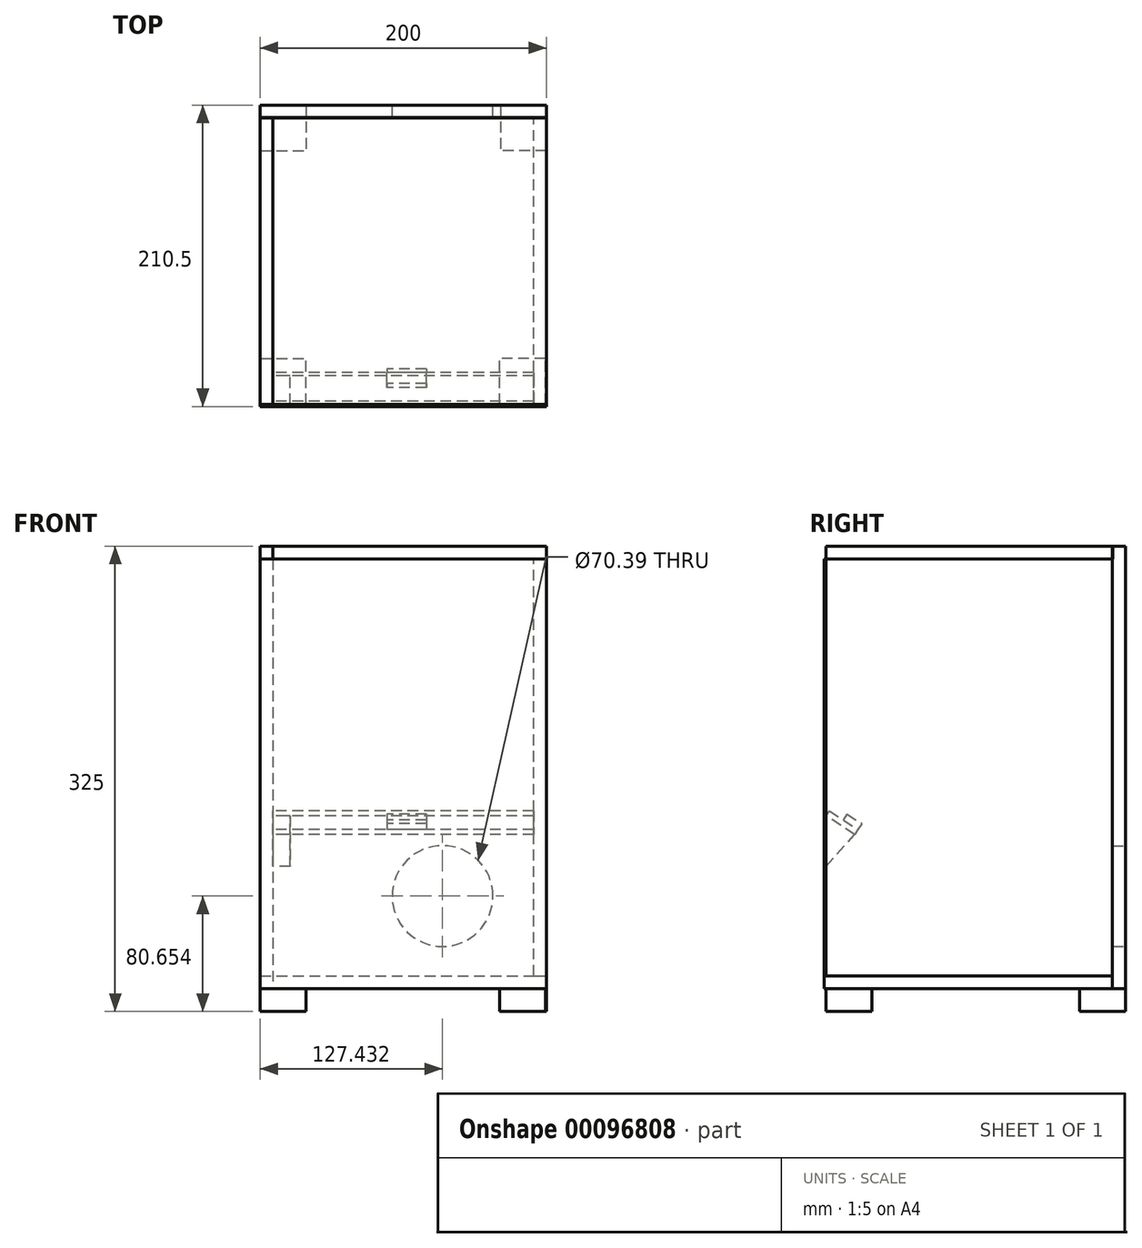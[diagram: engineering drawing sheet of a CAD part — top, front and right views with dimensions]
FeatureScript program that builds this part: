
annotation { "Feature Type Name" : "Feature", "Feature Type Description" : "" }
export const myFeature = defineFeature(function(context is Context, id is Id, definition is map)
    precondition{}
    {
        {
            var Q0;
            Q0=qCreatedBy(makeId("Front.planeOp"),FACE);
            var sketch = newSketch(context, id + "F0", { "sketchPlane" : qUnion([Q0])});
            skLineSegment(sketch, "E0.bottom", {"start": v(0, 0) * mm, "end": v(200, 0) * mm});
            skLineSegment(sketch, "E0.top", {"start": v(0, 300) * mm, "end": v(200, 300) * mm});
            skLineSegment(sketch, "E0.left", {"start": v(0, 0) * mm, "end": v(0, 300) * mm});
            skLineSegment(sketch, "E0.right", {"start": v(200, 0) * mm, "end": v(200, 300) * mm});
            skSolve(sketch);
        }
        {
            var Q0;
            Q0=makeQuery(id+"F0.imprint","IMPRINT",FACE,{"disambiguationData":[TD([[makeQuery(id+"F0.imprint","IMPRINT",EDGE,{"derivedFrom":sQuery(id+"F0.wireOp",EDGE,"E0.bottom")}),1.0]])]});
            var Q1;
            Q1=makeQuery(id+"F0.imprint","IMPRINT",FACE,{"disambiguationData":[TD([[makeQuery(id+"F0.imprint","IMPRINT",EDGE,{"derivedFrom":sQuery(id+"F0.wireOp",EDGE,"E0.bottom")}),1.0]])]});
            extrude(context, id + "F1", {"entities" : qUnion([Q0, Q1]), "depth" : 1.5 * mm});
        }
        {
            var Q0;
            Q0=makeQuery(id+"F1.opExtrude","CAP_FACE",FACE,{"disambiguationData":[OSD([sQuery(id+"F0.wireOp",EDGE,"E0.bottom"),sQuery(id+"F0.wireOp",EDGE,"E0.top"),sQuery(id+"F0.wireOp",EDGE,"E0.left"),sQuery(id+"F0.wireOp",EDGE,"E0.right")])],"isStart":true});
            var sketch = newSketch(context, id + "F2", { "sketchPlane" : qUnion([Q0])});
            skLineSegment(sketch, "E1.bottom", {"start": v(0, 300) * mm, "end": v(-9, 300) * mm});
            skLineSegment(sketch, "E1.top", {"start": v(0, 0) * mm, "end": v(-9, 0) * mm});
            skLineSegment(sketch, "E1.left", {"start": v(0, 300) * mm, "end": v(0, 0) * mm});
            skLineSegment(sketch, "E1.right", {"start": v(-9, 300) * mm, "end": v(-9, 0) * mm});
            skSolve(sketch);
        }
        {
            var Q0;
            Q0 = qSketchRegion(id + "F2", true);
            extrude(context, id + "F3", {"entities" : qUnion([Q0]), "depth" : 200 * mm});
        }
        {
            var Q0;
            Q0=makeQuery(id+"F3.opExtrude","SWEPT_FACE",FACE,{"disambiguationData":[OSD([sQuery(id+"F2.wireOp",EDGE,"E1.right")])]});
            var sketch = newSketch(context, id + "F4", { "sketchPlane" : qUnion([Q0])});
            skLineSegment(sketch, "E2", {"start": v(0, 120.62) * mm, "end": v(0, 85.37) * mm});
            skLineSegment(sketch, "E3", {"start": v(0, 85.37) * mm, "end": v(19.83, 107.63) * mm});
            skLineSegment(sketch, "E4", {"start": v(19.83, 107.63) * mm, "end": v(0, 120.62) * mm});
            skSolve(sketch);
        }
        {
            var Q0;
            Q0 = qSketchRegion(id + "F4", true);
            extrude(context, id + "F5", {"entities" : qUnion([Q0]), "depth" : 12 * mm});
        }
        {
            var Q0;
            Q0=makeQuery(id+"F3.opExtrude","SWEPT_FACE",FACE,{"disambiguationData":[OSD([sQuery(id+"F2.wireOp",EDGE,"E1.right")])]});
            var sketch = newSketch(context, id + "F6", { "sketchPlane" : qUnion([Q0])});
            skLineSegment(sketch, "E5", {"start": v(19.83, 107.63) * mm, "end": v(0, 120.62) * mm});
            skLineSegment(sketch, "E6", {"start": v(0, 120.62) * mm, "end": v(2.3, 124.14) * mm});
            skLineSegment(sketch, "E7", {"start": v(2.3, 124.14) * mm, "end": v(22.14, 111.15) * mm});
            skLineSegment(sketch, "E8", {"start": v(22.14, 111.15) * mm, "end": v(19.83, 107.63) * mm});
            skSolve(sketch);
        }
        {
            var Q0;
            Q0=makeQuery(id+"F6.imprint","IMPRINT",FACE,{"disambiguationData":[TD([[makeQuery(id+"F6.imprint","IMPRINT",EDGE,{"derivedFrom":sQuery(id+"F6.wireOp",EDGE,"E5")}),-1.0]])]});
            extrude(context, id + "F7", {"entities" : qUnion([Q0]), "depth" : 182 * mm});
        }
        {
            var Q0;
            Q0=makeQuery(id+"F7.opExtrude","SWEPT_FACE",FACE,{"disambiguationData":[OSD([sQuery(id+"F6.wireOp",EDGE,"E7")])]});
            var sketch = newSketch(context, id + "F8", { "sketchPlane" : qUnion([Q0])});
            skLineSegment(sketch, "E9.bottom", {"start": v(116.04, -54.62) * mm, "end": v(88.6, -54.62) * mm});
            skLineSegment(sketch, "E9.top", {"start": v(116.04, -42.37) * mm, "end": v(88.6, -42.37) * mm});
            skLineSegment(sketch, "E9.left", {"start": v(116.04, -54.62) * mm, "end": v(116.04, -42.37) * mm});
            skLineSegment(sketch, "E9.right", {"start": v(88.6, -54.62) * mm, "end": v(88.6, -42.37) * mm});
            skSolve(sketch);
        }
        {
            var Q0;
            Q0 = qSketchRegion(id + "F8", true);
            extrude(context, id + "F9", {"entities" : qUnion([Q0]), "depth" : 5 * mm});
        }
        {
            var Q0;
            Q0=makeQuery(id+"F3.opExtrude","SWEPT_FACE",FACE,{"disambiguationData":[OSD([sQuery(id+"F2.wireOp",EDGE,"E1.top")])]});
            var sketch = newSketch(context, id + "F10", { "sketchPlane" : qUnion([Q0])});
            skLineSegment(sketch, "E10.bottom", {"start": v(0, 0) * mm, "end": v(200, 0) * mm});
            skLineSegment(sketch, "E10.top", {"start": v(0, -200) * mm, "end": v(200, -200) * mm});
            skLineSegment(sketch, "E10.left", {"start": v(0, 0) * mm, "end": v(0, -200) * mm});
            skLineSegment(sketch, "E10.right", {"start": v(200, 0) * mm, "end": v(200, -200) * mm});
            skSolve(sketch);
        }
        {
            var Q0;
            Q0 = qSketchRegion(id + "F10", true);
            extrude(context, id + "F11", {"entities" : qUnion([Q0]), "oppositeDirection" : true, "depth" : 9 * mm});
        }
        {
            var Q0;
            Q0=makeQuery(id+"F11.opExtrude","SWEPT_FACE",FACE,{"disambiguationData":[OSD([sQuery(id+"F10.wireOp",EDGE,"E10.right")])]});
            var sketch = newSketch(context, id + "F12", { "sketchPlane" : qUnion([Q0])});
            skLineSegment(sketch, "E11.bottom", {"start": v(0, 0) * mm, "end": v(200, 0) * mm});
            skLineSegment(sketch, "E11.top", {"start": v(0, 300) * mm, "end": v(200, 300) * mm});
            skLineSegment(sketch, "E11.left", {"start": v(0, 0) * mm, "end": v(0, 300) * mm});
            skLineSegment(sketch, "E11.right", {"start": v(200, 0) * mm, "end": v(200, 300) * mm});
            skSolve(sketch);
        }
        {
            var Q0;
            {var subQ0=sQuery(id+"F12.wireOp",EDGE,"E11.top");Q0=makeQuery(id+"F12.imprint","IMPRINT",FACE,{"disambiguationData":[TD([[makeQuery(id+"F12.imprint","IMPRINT",EDGE,{"derivedFrom":subQ0}),-1.0]])]});}
            extrude(context, id + "F13", {"entities" : qUnion([Q0]), "oppositeDirection" : true, "depth" : 9 * mm});
        }
        {
            var Q0;
            Q0=makeQuery(id+"F3.opExtrude","SWEPT_FACE",FACE,{"disambiguationData":[OSD([sQuery(id+"F2.wireOp",EDGE,"E1.bottom")])]});
            var sketch = newSketch(context, id + "F14", { "sketchPlane" : qUnion([Q0])});
            skLineSegment(sketch, "E12.bottom", {"start": v(0, 0) * mm, "end": v(200, 0) * mm});
            skLineSegment(sketch, "E12.top", {"start": v(0, 200.17) * mm, "end": v(200, 200.17) * mm});
            skLineSegment(sketch, "E12.left", {"start": v(0, 0) * mm, "end": v(0, 200.17) * mm});
            skLineSegment(sketch, "E12.right", {"start": v(200, 0) * mm, "end": v(200, 200.17) * mm});
            skSolve(sketch);
        }
        {
            var Q0;
            {var subQ4=sQuery(id+"F14.wireOp",EDGE,"E12.top");Q0=makeQuery(id+"F14.imprint","IMPRINT",FACE,{"disambiguationData":[TD([[makeQuery(id+"F14.imprint","IMPRINT",EDGE,{"derivedFrom":subQ4}),-1.0]])]});}
            extrude(context, id + "F15", {"entities" : qUnion([Q0]), "depth" : 9 * mm});
        }
        {
            var Q0;
            Q0=makeQuery(id+"F11.opExtrude","SWEPT_FACE",FACE,{"disambiguationData":[OSD([sQuery(id+"F10.wireOp",EDGE,"E10.top")])]});
            var sketch = newSketch(context, id + "F16", { "sketchPlane" : qUnion([Q0])});
            skLineSegment(sketch, "E13.bottom", {"start": v(0, 0) * mm, "end": v(-200, 0) * mm});
            skLineSegment(sketch, "E13.top", {"start": v(0, 309) * mm, "end": v(-200, 309) * mm});
            skLineSegment(sketch, "E13.left", {"start": v(0, 0) * mm, "end": v(0, 309) * mm});
            skLineSegment(sketch, "E13.right", {"start": v(-200, 0) * mm, "end": v(-200, 309) * mm});
            skSolve(sketch);
        }
        {
            var Q0;
            Q0 = qSketchRegion(id + "F16", true);
            extrude(context, id + "F17", {"entities" : qUnion([Q0]), "depth" : 9 * mm});
        }
        {
            var Q0;
            {var subQ0=sQuery(id+"F10.wireOp",EDGE,"E10.left");Q0=makeQuery(id+"F10.imprint","IMPRINT",FACE,{"disambiguationData":[TD([[makeQuery(id+"F10.imprint","IMPRINT",EDGE,{"derivedFrom":subQ0}),-1.0]])]});}
            var sketch = newSketch(context, id + "F18", { "sketchPlane" : qUnion([Q0])});
            skLineSegment(sketch, "E14.bottom", {"start": v(0, 0) * mm, "end": v(32, 0) * mm});
            skLineSegment(sketch, "E14.top", {"start": v(0, -32) * mm, "end": v(32, -32) * mm});
            skLineSegment(sketch, "E14.left", {"start": v(0, 0) * mm, "end": v(0, -32) * mm});
            skLineSegment(sketch, "E14.right", {"start": v(32, 0) * mm, "end": v(32, -32) * mm});
            skSolve(sketch);
        }
        {
            var Q0;
            Q0 = qSketchRegion(id + "F18", true);
            extrude(context, id + "F19", {"entities" : qUnion([Q0]), "depth" : 16 * mm});
        }
        {
            var Q0;
            {var subQ2=sQuery(id+"F10.wireOp",EDGE,"E10.right");Q0=makeQuery(id+"F10.imprint","IMPRINT",FACE,{"disambiguationData":[TD([[makeQuery(id+"F10.imprint","IMPRINT",EDGE,{"derivedFrom":subQ2}),-1.0]])]});}
            var sketch = newSketch(context, id + "F20", { "sketchPlane" : qUnion([Q0])});
            skLineSegment(sketch, "E15.bottom", {"start": v(199.26, 0) * mm, "end": v(167.26, 0) * mm});
            skLineSegment(sketch, "E15.top", {"start": v(199.26, -32) * mm, "end": v(167.26, -32) * mm});
            skLineSegment(sketch, "E15.left", {"start": v(199.26, 0) * mm, "end": v(199.26, -32) * mm});
            skLineSegment(sketch, "E15.right", {"start": v(167.26, 0) * mm, "end": v(167.26, -32) * mm});
            skSolve(sketch);
        }
        {
            var Q0;
            Q0 = qSketchRegion(id + "F20", true);
            extrude(context, id + "F21", {"entities" : qUnion([Q0]), "operationType" : NewBodyOperationType.ADD, "depth" : 16 * mm});
        }
        {
            var Q0;
            Q0=makeQuery(id+"F17.opExtrude","SWEPT_FACE",FACE,{"disambiguationData":[OSD([sQuery(id+"F16.wireOp",EDGE,"E13.bottom")])]});
            var sketch = newSketch(context, id + "F22", { "sketchPlane" : qUnion([Q0])});
            skLineSegment(sketch, "E16.bottom", {"start": v(0, -209) * mm, "end": v(32, -209) * mm});
            skLineSegment(sketch, "E16.top", {"start": v(0, -177) * mm, "end": v(32, -177) * mm});
            skLineSegment(sketch, "E16.left", {"start": v(0, -209) * mm, "end": v(0, -177) * mm});
            skLineSegment(sketch, "E16.right", {"start": v(32, -209) * mm, "end": v(32, -177) * mm});
            skSolve(sketch);
        }
        {
            var Q0;
            Q0 = qSketchRegion(id + "F22", true);
            extrude(context, id + "F23", {"entities" : qUnion([Q0]), "depth" : 16 * mm});
        }
        {
            var Q0;
            Q0=makeQuery(id+"F17.opExtrude","SWEPT_FACE",FACE,{"disambiguationData":[OSD([sQuery(id+"F16.wireOp",EDGE,"E13.bottom")])]});
            var sketch = newSketch(context, id + "F24", { "sketchPlane" : qUnion([Q0])});
            skLineSegment(sketch, "E17.bottom", {"start": v(200, -209) * mm, "end": v(168, -209) * mm});
            skLineSegment(sketch, "E17.top", {"start": v(200, -177) * mm, "end": v(168, -177) * mm});
            skLineSegment(sketch, "E17.left", {"start": v(200, -209) * mm, "end": v(200, -177) * mm});
            skLineSegment(sketch, "E17.right", {"start": v(168, -209) * mm, "end": v(168, -177) * mm});
            skSolve(sketch);
        }
        {
            var Q0;
            Q0 = qSketchRegion(id + "F24", true);
            extrude(context, id + "F25", {"entities" : qUnion([Q0]), "depth" : 16 * mm});
        }
        {
            var Q0;
            Q0=makeQuery(id+"F17.opExtrude","CAP_FACE",FACE,{"disambiguationData":[OSD([sQuery(id+"F16.wireOp",EDGE,"E13.bottom"),sQuery(id+"F16.wireOp",EDGE,"E13.top"),sQuery(id+"F16.wireOp",EDGE,"E13.left"),sQuery(id+"F16.wireOp",EDGE,"E13.right")])],"isStart":false});
            var sketch = newSketch(context, id + "F26", { "sketchPlane" : qUnion([Q0])});
            skCircle(sketch, "E18", {"center": v(-127.43, 64.65) * mm, "radius": 35.2 * mm});
            skSolve(sketch);
        }
        {
            var Q0;
            Q0 = qSketchRegion(id + "F26", true);
            extrude(context, id + "F27", {"entities" : qUnion([Q0]), "operationType" : NewBodyOperationType.REMOVE, "oppositeDirection" : true, "depth" : 9 * mm});
        }
    });
